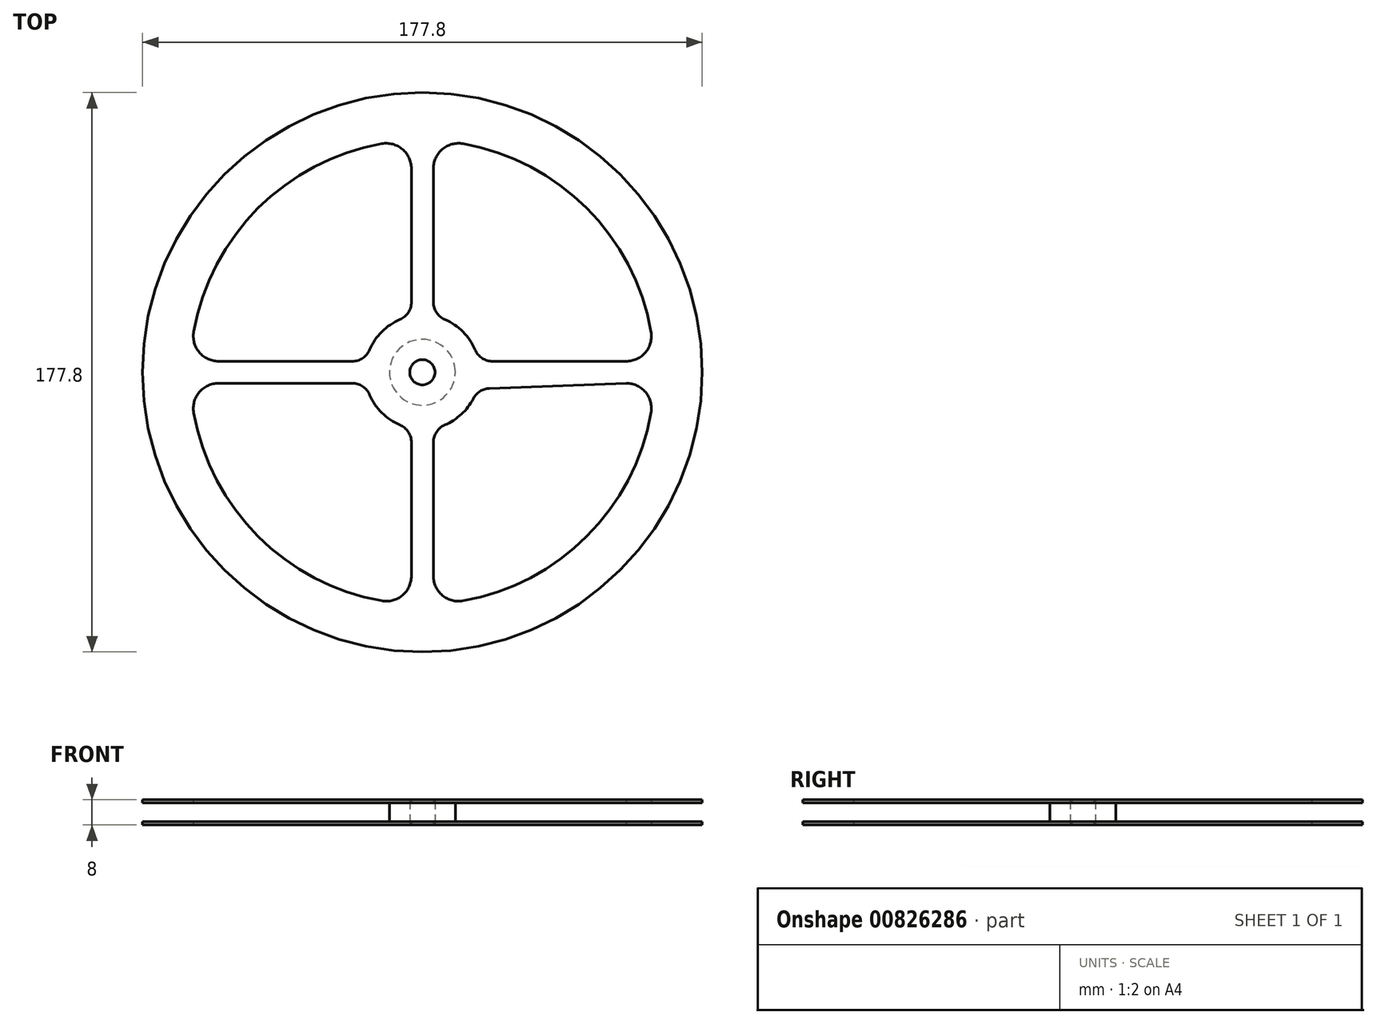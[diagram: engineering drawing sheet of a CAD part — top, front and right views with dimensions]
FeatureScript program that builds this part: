
annotation { "Feature Type Name" : "Feature", "Feature Type Description" : "" }
export const myFeature = defineFeature(function(context is Context, id is Id, definition is map)
    precondition{}
    {
        {
            var Q0;
            Q0=qCreatedBy(makeId("Top.planeOp"),FACE);
            var sketch = newSketch(context, id + "F0", { "sketchPlane" : qUnion([Q0])});
            skCircle(sketch, "E0", {"center": v(0, 0) * mm, "radius": 88.9 * mm});
            skArc(sketch, "E1", {"start": v(-12.9, 72.65) * mm, "mid": v(-52.17, 52.17) * mm, "end": v(-72.65, 12.9) * mm});
            skLineSegment(sketch, "E2", {"start": v(-64.77, 3.5) * mm, "end": v(-22.27, 3.5) * mm});
            skLineSegment(sketch, "E3", {"start": v(-3.5, 64.77) * mm, "end": v(-3.5, 22.27) * mm});
            skLineSegment(sketch, "E4.MirrorCS", {"start": v(-64.77, -3.5) * mm, "end": v(-22.27, -3.5) * mm});
            skLineSegment(sketch, "E5.MirrorCS", {"start": v(3.5, 64.77) * mm, "end": v(3.5, 22.27) * mm});
            skArc(sketch, "E6.trimOffspring", {"start": v(72.65, 12.9) * mm, "mid": v(52.17, 52.17) * mm, "end": v(12.9, 72.65) * mm});
            skArc(sketch, "E7.trimOffspring", {"start": v(12.9, -72.65) * mm, "mid": v(52.17, -52.17) * mm, "end": v(72.65, -12.9) * mm});
            skArc(sketch, "E8.trimOffspring", {"start": v(-72.65, -12.9) * mm, "mid": v(-52.17, -52.17) * mm, "end": v(-12.9, -72.65) * mm});
            skPoint(sketch, "E9.visualSharp", {"position": v(-3.5, 73.7) * mm});
            skArc(sketch, "E9.filletArc", {"start": v(-3.5, 64.77) * mm, "mid": v(-6.36, 70.9) * mm, "end": v(-12.9, 72.65) * mm});
            skPoint(sketch, "E10.visualSharp", {"position": v(3.5, 73.7) * mm});
            skArc(sketch, "E10.filletArc", {"start": v(12.9, 72.65) * mm, "mid": v(6.36, 70.9) * mm, "end": v(3.5, 64.77) * mm});
            skPoint(sketch, "E11.visualSharp", {"position": v(73.7, 3.5) * mm});
            skArc(sketch, "E11.filletArc", {"start": v(64.77, 3.5) * mm, "mid": v(70.9, 6.36) * mm, "end": v(72.65, 12.9) * mm});
            skPoint(sketch, "E12.visualSharp", {"position": v(73.7, -3.5) * mm});
            skArc(sketch, "E12.filletArc", {"start": v(72.65, -12.9) * mm, "mid": v(70.9, -6.36) * mm, "end": v(64.77, -3.5) * mm});
            skPoint(sketch, "E13.visualSharp", {"position": v(3.5, -73.7) * mm});
            skArc(sketch, "E13.filletArc", {"start": v(3.5, -64.77) * mm, "mid": v(6.36, -70.9) * mm, "end": v(12.9, -72.65) * mm});
            skPoint(sketch, "E14.visualSharp", {"position": v(-3.5, -73.7) * mm});
            skArc(sketch, "E14.filletArc", {"start": v(-12.9, -72.65) * mm, "mid": v(-6.36, -70.9) * mm, "end": v(-3.5, -64.77) * mm});
            skPoint(sketch, "E15.visualSharp", {"position": v(-73.7, -3.5) * mm});
            skArc(sketch, "E15.filletArc", {"start": v(-64.77, -3.5) * mm, "mid": v(-70.9, -6.36) * mm, "end": v(-72.65, -12.9) * mm});
            skPoint(sketch, "E16.visualSharp", {"position": v(-73.7, 3.5) * mm});
            skArc(sketch, "E16.filletArc", {"start": v(-72.65, 12.9) * mm, "mid": v(-70.9, 6.36) * mm, "end": v(-64.77, 3.5) * mm});
            skArc(sketch, "E17", {"start": v(16.75, 7.15) * mm, "mid": v(12.88, 12.88) * mm, "end": v(7.15, 16.75) * mm});
            skLineSegment(sketch, "E18.trimOffspring", {"start": v(3.5, -22.27) * mm, "end": v(3.5, -64.77) * mm});
            skLineSegment(sketch, "E19.trimOffspring", {"start": v(-3.5, -22.27) * mm, "end": v(-3.5, -64.77) * mm});
            skLineSegment(sketch, "E20.trimOffspring", {"start": v(22.27, 3.5) * mm, "end": v(64.77, 3.5) * mm});
            skLineSegment(sketch, "E21.trimOffspring", {"start": v(21.3, -5.11) * mm, "end": v(64.77, -3.5) * mm});
            skCircle(sketch, "E22", {"center": v(0, 0) * mm, "radius": 4 * mm});
            skArc(sketch, "E23.trimOffspring", {"start": v(7.15, -16.75) * mm, "mid": v(12.4, -13.34) * mm, "end": v(16.18, -8.36) * mm});
            skArc(sketch, "E24.trimOffspring", {"start": v(-16.75, -7.15) * mm, "mid": v(-12.88, -12.88) * mm, "end": v(-7.15, -16.75) * mm});
            skArc(sketch, "E25.trimOffspring", {"start": v(-7.15, 16.75) * mm, "mid": v(-12.88, 12.88) * mm, "end": v(-16.75, 7.15) * mm});
            skPoint(sketch, "E26.visualSharp", {"position": v(-3.5, 17.88) * mm});
            skArc(sketch, "E26.filletArc", {"start": v(-7.15, 16.75) * mm, "mid": v(-4.5, 18.97) * mm, "end": v(-3.5, 22.27) * mm});
            skPoint(sketch, "E27.visualSharp", {"position": v(17.88, 3.5) * mm});
            skArc(sketch, "E27.filletArc", {"start": v(16.75, 7.15) * mm, "mid": v(18.97, 4.5) * mm, "end": v(22.27, 3.5) * mm});
            skPoint(sketch, "E28.visualSharp", {"position": v(17.44, -5.26) * mm});
            skArc(sketch, "E28.filletArc", {"start": v(21.3, -5.11) * mm, "mid": v(18.3, -6.04) * mm, "end": v(16.18, -8.36) * mm});
            skPoint(sketch, "E29.visualSharp", {"position": v(3.5, -17.88) * mm});
            skArc(sketch, "E29.filletArc", {"start": v(7.15, -16.75) * mm, "mid": v(4.5, -18.97) * mm, "end": v(3.5, -22.27) * mm});
            skPoint(sketch, "E30.visualSharp", {"position": v(-3.5, -17.88) * mm});
            skArc(sketch, "E30.filletArc", {"start": v(-3.5, -22.27) * mm, "mid": v(-4.5, -18.97) * mm, "end": v(-7.15, -16.75) * mm});
            skPoint(sketch, "E31.visualSharp", {"position": v(-17.88, -3.5) * mm});
            skArc(sketch, "E31.filletArc", {"start": v(-16.75, -7.15) * mm, "mid": v(-18.97, -4.5) * mm, "end": v(-22.27, -3.5) * mm});
            skPoint(sketch, "E32.visualSharp", {"position": v(-17.88, 3.5) * mm});
            skArc(sketch, "E32.filletArc", {"start": v(-22.27, 3.5) * mm, "mid": v(-18.97, 4.5) * mm, "end": v(-16.75, 7.15) * mm});
            skPoint(sketch, "E33.visualSharp", {"position": v(3.5, 17.88) * mm});
            skArc(sketch, "E33.filletArc", {"start": v(3.5, 22.27) * mm, "mid": v(4.5, 18.97) * mm, "end": v(7.15, 16.75) * mm});
            skCircle(sketch, "E34", {"center": v(0, 0) * mm, "radius": 10.46 * mm});
            skSolve(sketch);
        }
        {
            var Q0;
            Q0=makeQuery(id+"F0.imprint","IMPRINT",FACE,{"disambiguationData":[TD([[makeQuery(id+"F0.imprint","IMPRINT",EDGE,{"derivedFrom":sQuery(id+"F0.wireOp",EDGE,"E0")}),1.0]])]});
            var Q1;
            Q1=makeQuery(id+"F0.imprint","IMPRINT",FACE,{"disambiguationData":[TD([[makeQuery(id+"F0.imprint","IMPRINT",EDGE,{"derivedFrom":sQuery(id+"F0.wireOp",EDGE,"E22")}),-1.0]])]});
            extrude(context, id + "F1", {"entities" : qUnion([Q0, Q1]), "depth" : 1 * mm, "offsetDistance" : 25 * mm});
        }
        {
            var Q0;
            Q0=qCreatedBy(makeId("Top.planeOp"),FACE);
            cPlane(context, id + "F2", {"entities" : qUnion([Q0]), "cplaneType" : CPlaneType.OFFSET, "offset" : 7 * mm, "width" : 150 * mm, "height" : 150 * mm});
        }
        {
            var Q0;
            Q0=qCreatedBy(id+"F2.planeOp",FACE);
            var sketch = newSketch(context, id + "F3", { "sketchPlane" : qUnion([Q0])});
            skCircle(sketch, "E35.0.0", {"center": v(0, 0) * mm, "radius": 88.9 * mm});
            skArc(sketch, "E36.0.0", {"start": v(-16.75, 7.15) * mm, "mid": v(-12.88, 12.88) * mm, "end": v(-7.15, 16.75) * mm});
            skArc(sketch, "E36.0.1", {"start": v(-7.15, 16.75) * mm, "mid": v(-4.5, 18.97) * mm, "end": v(-3.5, 22.27) * mm});
            skLineSegment(sketch, "E36.0.2", {"start": v(-3.5, 22.27) * mm, "end": v(-3.5, 64.77) * mm});
            skArc(sketch, "E36.0.3", {"start": v(-3.5, 64.77) * mm, "mid": v(-6.36, 70.9) * mm, "end": v(-12.9, 72.65) * mm});
            skArc(sketch, "E36.0.4", {"start": v(-12.9, 72.65) * mm, "mid": v(-52.17, 52.17) * mm, "end": v(-72.65, 12.9) * mm});
            skArc(sketch, "E36.0.5", {"start": v(-72.65, 12.9) * mm, "mid": v(-70.9, 6.36) * mm, "end": v(-64.77, 3.5) * mm});
            skLineSegment(sketch, "E36.0.6", {"start": v(-64.77, 3.5) * mm, "end": v(-22.27, 3.5) * mm});
            skArc(sketch, "E36.0.7", {"start": v(-22.27, 3.5) * mm, "mid": v(-18.97, 4.5) * mm, "end": v(-16.75, 7.15) * mm});
            skLineSegment(sketch, "E37.0.0", {"start": v(-3.5, -64.77) * mm, "end": v(-3.5, -22.27) * mm});
            skArc(sketch, "E37.0.1", {"start": v(-3.5, -22.27) * mm, "mid": v(-4.5, -18.97) * mm, "end": v(-7.15, -16.75) * mm});
            skArc(sketch, "E37.0.2", {"start": v(-7.15, -16.75) * mm, "mid": v(-12.88, -12.88) * mm, "end": v(-16.75, -7.15) * mm});
            skArc(sketch, "E37.0.3", {"start": v(-16.75, -7.15) * mm, "mid": v(-18.97, -4.5) * mm, "end": v(-22.27, -3.5) * mm});
            skLineSegment(sketch, "E37.0.4", {"start": v(-22.27, -3.5) * mm, "end": v(-64.77, -3.5) * mm});
            skArc(sketch, "E37.0.5", {"start": v(-64.77, -3.5) * mm, "mid": v(-70.9, -6.36) * mm, "end": v(-72.65, -12.9) * mm});
            skArc(sketch, "E37.0.6", {"start": v(-72.65, -12.9) * mm, "mid": v(-52.17, -52.17) * mm, "end": v(-12.9, -72.65) * mm});
            skArc(sketch, "E37.0.7", {"start": v(-12.9, -72.65) * mm, "mid": v(-6.36, -70.9) * mm, "end": v(-3.5, -64.77) * mm});
            skArc(sketch, "E38.0.0", {"start": v(16.18, -8.36) * mm, "mid": v(12.4, -13.34) * mm, "end": v(7.15, -16.75) * mm});
            skArc(sketch, "E38.0.1", {"start": v(7.15, -16.75) * mm, "mid": v(4.5, -18.97) * mm, "end": v(3.5, -22.27) * mm});
            skLineSegment(sketch, "E38.0.2", {"start": v(3.5, -22.27) * mm, "end": v(3.5, -64.77) * mm});
            skArc(sketch, "E38.0.3", {"start": v(3.5, -64.77) * mm, "mid": v(6.36, -70.9) * mm, "end": v(12.9, -72.65) * mm});
            skArc(sketch, "E38.0.4", {"start": v(12.9, -72.65) * mm, "mid": v(52.17, -52.17) * mm, "end": v(72.65, -12.9) * mm});
            skArc(sketch, "E38.0.5", {"start": v(72.65, -12.9) * mm, "mid": v(70.9, -6.36) * mm, "end": v(64.77, -3.5) * mm});
            skLineSegment(sketch, "E38.0.6", {"start": v(64.77, -3.5) * mm, "end": v(21.3, -5.11) * mm});
            skArc(sketch, "E38.0.7", {"start": v(21.3, -5.11) * mm, "mid": v(18.3, -6.04) * mm, "end": v(16.18, -8.36) * mm});
            skArc(sketch, "E39.0.0", {"start": v(7.15, 16.75) * mm, "mid": v(12.88, 12.88) * mm, "end": v(16.75, 7.15) * mm});
            skArc(sketch, "E39.0.1", {"start": v(16.75, 7.15) * mm, "mid": v(18.97, 4.5) * mm, "end": v(22.27, 3.5) * mm});
            skLineSegment(sketch, "E39.0.2", {"start": v(22.27, 3.5) * mm, "end": v(64.77, 3.5) * mm});
            skArc(sketch, "E39.0.3", {"start": v(64.77, 3.5) * mm, "mid": v(70.9, 6.36) * mm, "end": v(72.65, 12.9) * mm});
            skArc(sketch, "E39.0.4", {"start": v(72.65, 12.9) * mm, "mid": v(52.17, 52.17) * mm, "end": v(12.9, 72.65) * mm});
            skArc(sketch, "E39.0.5", {"start": v(12.9, 72.65) * mm, "mid": v(6.36, 70.9) * mm, "end": v(3.5, 64.77) * mm});
            skLineSegment(sketch, "E39.0.6", {"start": v(3.5, 64.77) * mm, "end": v(3.5, 22.27) * mm});
            skArc(sketch, "E39.0.7", {"start": v(3.5, 22.27) * mm, "mid": v(4.5, 18.97) * mm, "end": v(7.15, 16.75) * mm});
            skCircle(sketch, "E40.0", {"center": v(0, 0) * mm, "radius": 4 * mm});
            skSolve(sketch);
        }
        {
            var Q0;
            Q0=makeQuery(id+"F0.imprint","IMPRINT",FACE,{"disambiguationData":[TD([[makeQuery(id+"F0.imprint","IMPRINT",EDGE,{"derivedFrom":sQuery(id+"F0.wireOp",EDGE,"E22")}),-1.0]])]});
            extrude(context, id + "F4", {"entities" : qUnion([Q0]), "operationType" : NewBodyOperationType.ADD, "depth" : 8 * mm, "offsetDistance" : 25 * mm});
        }
        {
            var Q0;
            Q0=makeQuery(id+"F3.imprint","IMPRINT",FACE,{"disambiguationData":[TD([[makeQuery(id+"F3.imprint","IMPRINT",EDGE,{"derivedFrom":sQuery(id+"F3.wireOp",EDGE,"E35.0.0")}),1.0]])]});
            extrude(context, id + "F5", {"entities" : qUnion([Q0]), "operationType" : NewBodyOperationType.ADD, "depth" : 1 * mm, "offsetDistance" : 25 * mm});
        }
    });
